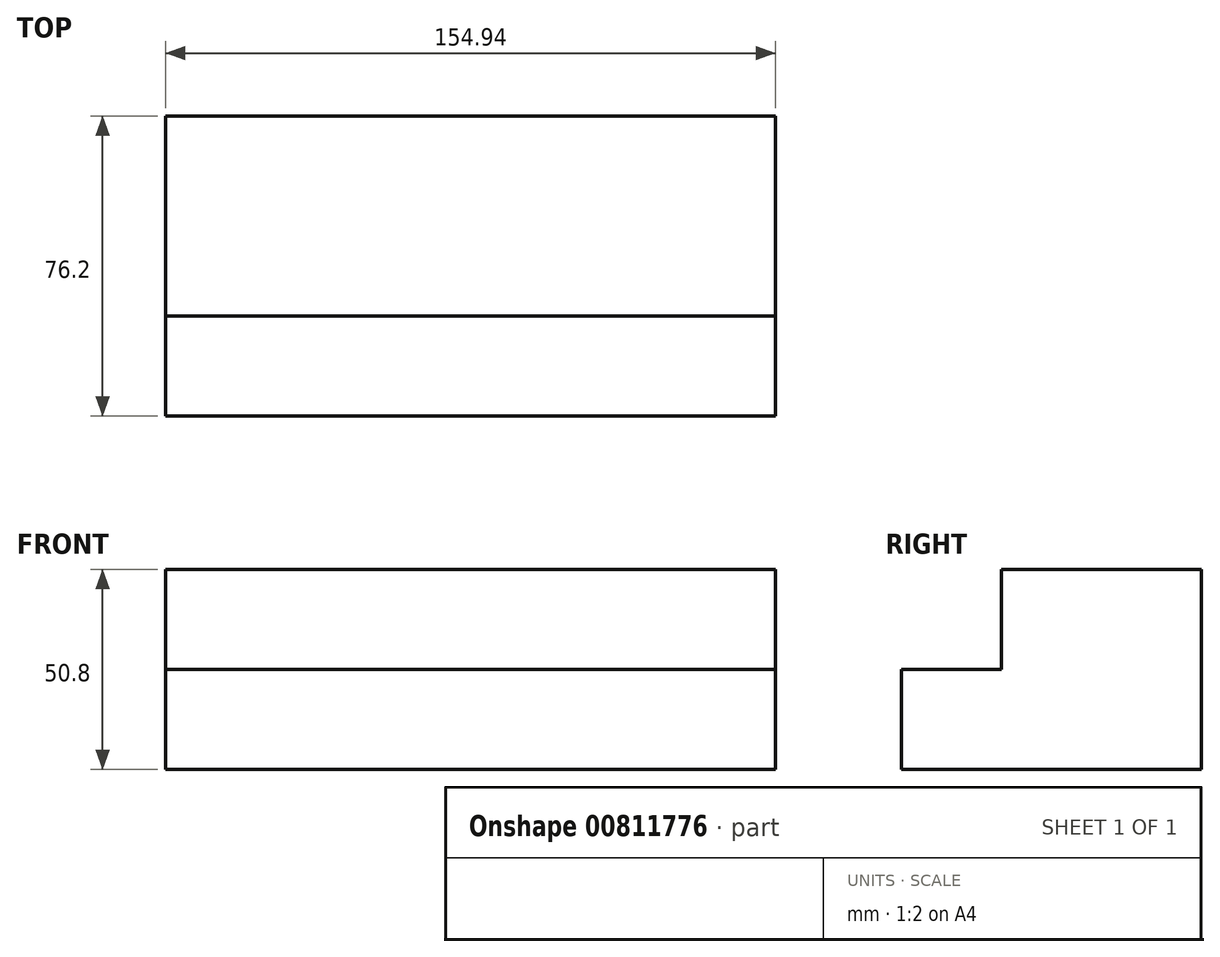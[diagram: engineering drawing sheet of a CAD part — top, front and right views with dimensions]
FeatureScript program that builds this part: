
annotation { "Feature Type Name" : "Feature", "Feature Type Description" : "" }
export const myFeature = defineFeature(function(context is Context, id is Id, definition is map)
    precondition{}
    {
        {
            var Q0;
            Q0=qCreatedBy(makeId("Right.planeOp"),FACE);
            var sketch = newSketch(context, id + "F0", { "sketchPlane" : qUnion([Q0])});
            skLineSegment(sketch, "E0", {"start": v(-52.35, 31.78) * mm, "end": v(-52.35, 6.38) * mm});
            skLineSegment(sketch, "E1", {"start": v(-52.35, 6.38) * mm, "end": v(23.85, 6.38) * mm});
            skLineSegment(sketch, "E2", {"start": v(23.85, 6.38) * mm, "end": v(23.85, 57.18) * mm});
            skLineSegment(sketch, "E3", {"start": v(23.85, 57.18) * mm, "end": v(-26.95, 57.18) * mm});
            skLineSegment(sketch, "E4", {"start": v(-26.95, 57.18) * mm, "end": v(-26.95, 31.78) * mm});
            skLineSegment(sketch, "E5", {"start": v(-26.95, 31.78) * mm, "end": v(-52.35, 31.78) * mm});
            skSolve(sketch);
        }
        {
            var Q0;
            Q0=makeQuery(id+"F0.imprint","IMPRINT",FACE,{"disambiguationData":[TD([[makeQuery(id+"F0.imprint","IMPRINT",EDGE,{"derivedFrom":sQuery(id+"F0.wireOp",EDGE,"E0")}),1.0]])]});
            extrude(context, id + "F1", {"entities" : qUnion([Q0]), "depth" : 154.94 * mm, "offsetDistance" : 25.4 * mm});
        }
    });
